# Revit family: Приточно-вытяжная система с рециркуляцией с водяным нагревом
name_source: partatom
category: Оборудование
units: mm (PartAtom-declared; Revit-internal decimal feet)

## family parameters
Всегда вертикально = Да
Классификация = Нет
На основе рабочей плоскости = Нет
Общий = Нет
При загрузке вырезать с полостями = Нет
Размер круглого соединителя = Использовать диаметр
Тип детали = Нормальный
Точка принадлежности помещению = Нет

## types (16) — shared parameters
ADSK_Напряжение = 380 В
ADSK_Свободный напор воздуха = 400.0 Па
Высота рамы = 120 мм
Длина гибкой встаки = 125 мм
Длина клапана FC = 120 мм
zero-valued in all types: Отметка по умолчанию

## per-type parameters (varying)
| type | ADSK_Размер_Высота | ADSK_Размер_Ширина | Высота ГВ | Ширина ГВ |
| 1А | 440 мм | 850 мм | 440 мм | 850 мм |
| 2А | 505 мм | 980 мм | 505 мм | 980 мм |
| 16B | 2580 мм | 2580 мм | 2580 мм | 2580 мм |
| 3A | 695 мм | 1080 мм | 695 мм | 1080 мм |
| 4A | 695 мм | 1360 мм | 695 мм | 1360 мм |
| 5A | 803 мм | 1360 мм | 803 мм | 1360 мм |
| 6A | 803 мм | 1580 мм | 803 мм | 1580 мм |
| 7A | 990 мм | 1580 мм | 990 мм | 1580 мм |
| 8A | 990 мм | 1950 мм | 990 мм | 1950 мм |
| 9A | 1095 мм | 2160 мм | 1095 мм | 2160 мм |
| 10B | 1360 мм | 2040 мм | 1360 мм | 2040 мм |
| 12B | 1680 мм | 2040 мм | 1680 мм | 2040 мм |
| 11B | 1360 мм | 2580 мм | 1360 мм | 2580 мм |
| 13B | 2040 мм | 2040 мм | 2040 мм | 2040 мм |
| 14B | 1680 мм | 2580 мм | 1680 мм | 2580 мм |
| 15B | 2040 мм | 2580 мм | 2040 мм | 2580 мм |
